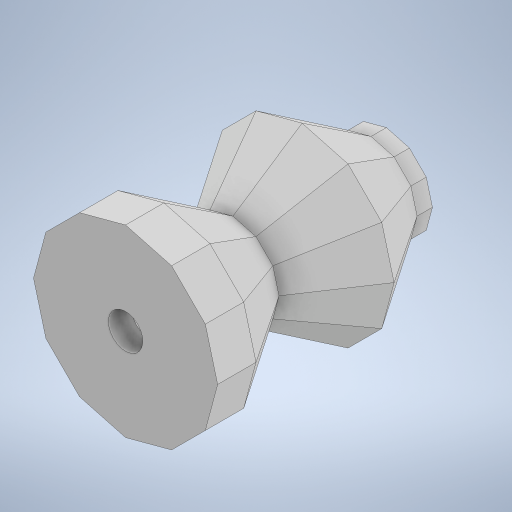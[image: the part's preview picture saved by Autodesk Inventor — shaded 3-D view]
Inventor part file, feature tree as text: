
AUTODESK INVENTOR PART (.ipt)
format: ipt  version: 2023 (Build 270158000, 158)  size: 354,304 bytes
history: native  units: in
note: dims shown in document units (in); Inventor stores cm internally (conversion verified against a paired STEP export)
features: sketch x6, extrude x4, projected_geometry x3, other x2, mirror x2, loft x1, shell x1
ambient origin geometry x8: Origin, YZ Plane, XZ Plane, XY Plane, X Axis, Y Axis, Z Axis, Center Point
bodies: Body1 (feature_tree)
feature tree (19):
  other  "솔리드1"
  sketch  "스케치1"
  other  "작업 평면1"
  loft  "로프트1"
  mirror  "미러1"
  mirror  "미러2"
  extrude  "돌출1"  Depth=0.3543in
  shell  "쉘6"  Thickness=0.4724in
  extrude  "돌출17"  TaperAngle=0.0deg  [1 undecoded]
  extrude  "돌출18"  TaperAngle=0.0deg  [1 undecoded]
  extrude  "돌출19"  Depth=0.1024in TaperAngle=0.0deg
  sketch  "스케치2"
  sketch  "스케치3"
  projected_geometry  "투영된 루프1"
  sketch  "스케치19"
  projected_geometry  "투영된 루프12"
  sketch  "스케치20"
  sketch  "스케치21"
  projected_geometry  "투영된 루프13"
note: 2 required parameter values undecoded (feature->parameter linkage not recoverable at this tier; creation-order binding heuristic only, values carry confidence <= 0.55)
